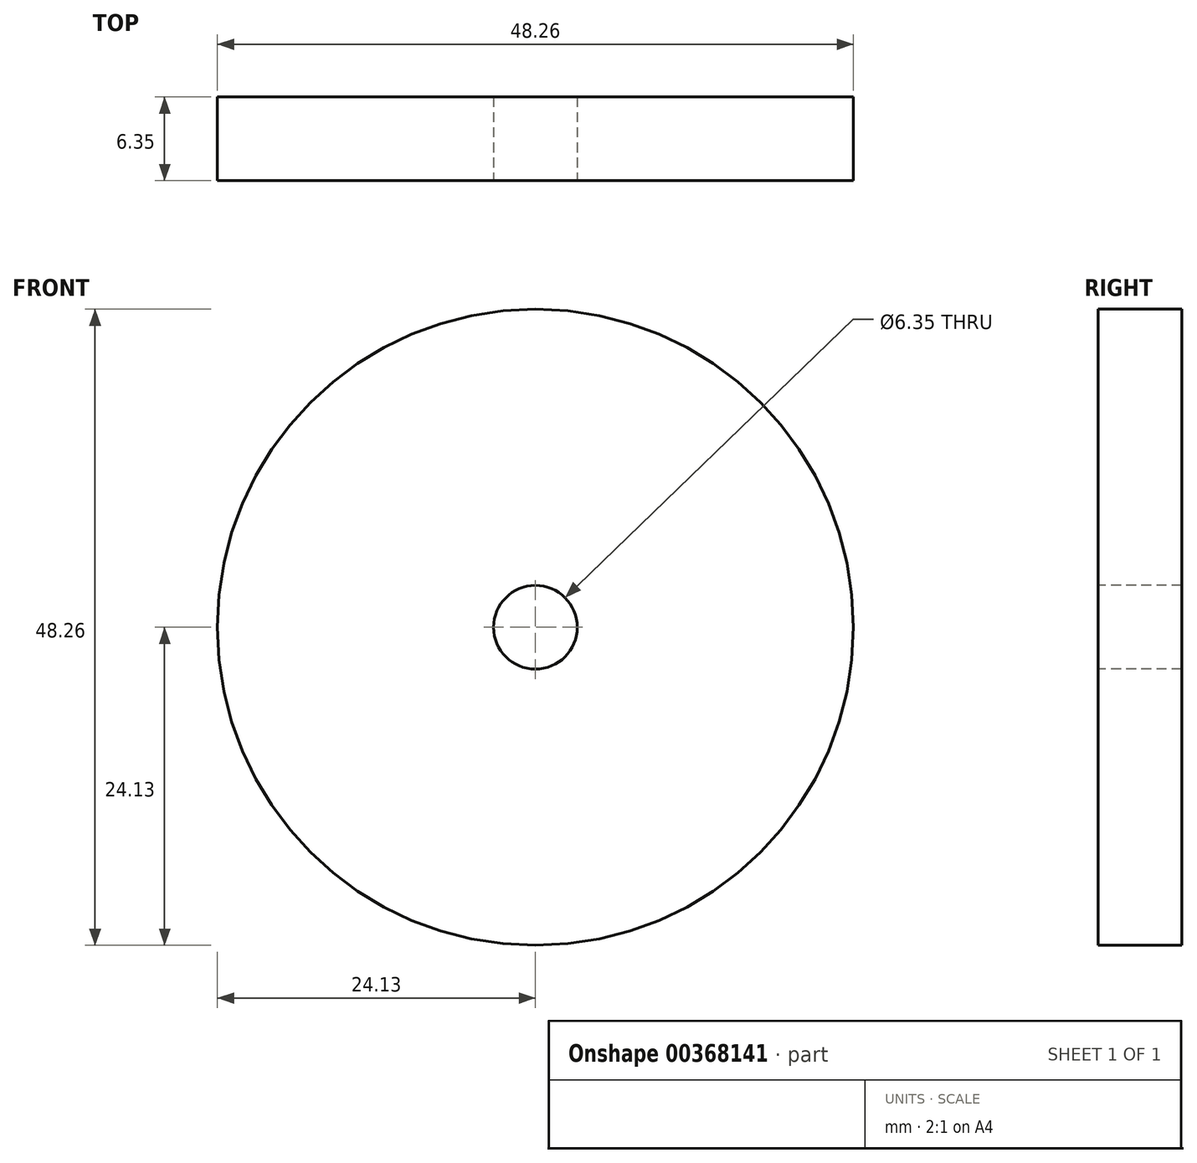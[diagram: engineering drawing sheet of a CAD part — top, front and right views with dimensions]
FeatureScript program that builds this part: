
annotation { "Feature Type Name" : "Feature", "Feature Type Description" : "" }
export const myFeature = defineFeature(function(context is Context, id is Id, definition is map)
    precondition{}
    {
        {
            var Q0;
            Q0=qCreatedBy(makeId("Front.planeOp"),FACE);
            var sketch = newSketch(context, id + "F0", { "sketchPlane" : qUnion([Q0])});
            skCircle(sketch, "E0", {"center": v(0, 0) * mm, "radius": 24.13 * mm});
            skSolve(sketch);
        }
        {
            var Q0;
            Q0 = qSketchRegion(id + "F0", true);
            extrude(context, id + "F1", {"entities" : qUnion([Q0]), "depth" : 6.35 * mm, "offsetDistance" : 25.4 * mm});
        }
        {
            var Q0;
            Q0=makeQuery(id+"F1.opExtrude","CAP_FACE",FACE,{"disambiguationData":[OSD([sQuery(id+"F0.wireOp",EDGE,"E0")])],"isStart":false});
            var sketch = newSketch(context, id + "F2", { "sketchPlane" : qUnion([Q0])});
            skCircle(sketch, "E1", {"center": v(0, 0) * mm, "radius": 3.18 * mm});
            skSolve(sketch);
        }
        {
            var Q0;
            Q0=makeQuery(id+"F2.imprint","IMPRINT",FACE,{"disambiguationData":[TD([[makeQuery(id+"F2.imprint","IMPRINT",EDGE,{"derivedFrom":sQuery(id+"F2.wireOp",EDGE,"E1")}),1.0]])]});
            extrude(context, id + "F3", {"entities" : qUnion([Q0]), "operationType" : NewBodyOperationType.REMOVE, "oppositeDirection" : true, "depth" : 6.35 * mm, "offsetDistance" : 25.4 * mm});
        }
    });
